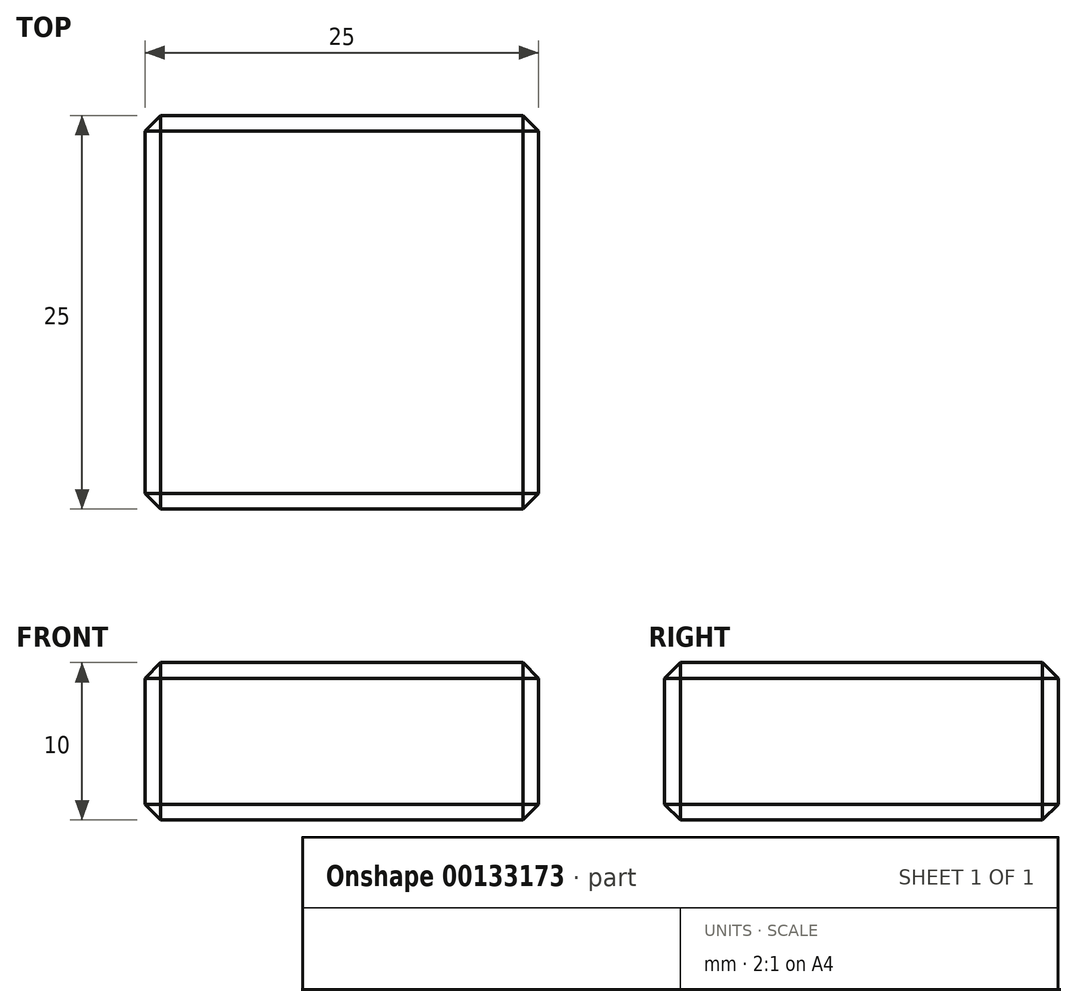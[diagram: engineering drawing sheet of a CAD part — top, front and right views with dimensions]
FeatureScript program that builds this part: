
annotation { "Feature Type Name" : "Feature", "Feature Type Description" : "" }
export const myFeature = defineFeature(function(context is Context, id is Id, definition is map)
    precondition{}
    {
        {
            var Q0;
            Q0=qCreatedBy(makeId("Front.planeOp"),FACE);
            var sketch = newSketch(context, id + "F0", { "sketchPlane" : qUnion([Q0])});
            skLineSegment(sketch, "E0.bottom", {"start": v(-30.6, 0) * mm, "end": v(-5.6, 0) * mm});
            skLineSegment(sketch, "E0.top", {"start": v(-30.6, 10) * mm, "end": v(-5.6, 10) * mm});
            skLineSegment(sketch, "E0.left", {"start": v(-30.6, 0) * mm, "end": v(-30.6, 10) * mm});
            skLineSegment(sketch, "E0.right", {"start": v(-5.6, 0) * mm, "end": v(-5.6, 10) * mm});
            skSolve(sketch);
        }
        {
            var Q0;
            Q0=makeQuery(id+"F0.imprint","IMPRINT",FACE,{"disambiguationData":[TD([[makeQuery(id+"F0.imprint","IMPRINT",EDGE,{"derivedFrom":sQuery(id+"F0.wireOp",EDGE,"E0.bottom")}),1.0]])]});
            extrude(context, id + "F1", {"entities" : qUnion([Q0]), "endBound" : BoundingType.SYMMETRIC, "depth" : 25 * mm});
        }
        {
            var Q0;
            Q0=makeQuery(id+"F1.opExtrude","CAP_EDGE",EDGE,{"disambiguationData":[OSD([sQuery(id+"F0.wireOp",EDGE,"E0.left")])],"isStart":false});
            var Q1;
            Q1=makeQuery(id+"F1.opExtrude","CAP_EDGE",EDGE,{"disambiguationData":[OSD([sQuery(id+"F0.wireOp",EDGE,"E0.right")])],"isStart":false});
            var Q2;
            Q2=makeQuery(id+"F1.opExtrude","CAP_EDGE",EDGE,{"disambiguationData":[OSD([sQuery(id+"F0.wireOp",EDGE,"E0.top")])],"isStart":false});
            var Q3;
            Q3=makeQuery(id+"F1.opExtrude","CAP_EDGE",EDGE,{"disambiguationData":[OSD([sQuery(id+"F0.wireOp",EDGE,"E0.bottom")])],"isStart":false});
            var Q4;
            Q4=makeQuery(id+"F1.opExtrude","SWEPT_EDGE",EDGE,{"disambiguationData":[OSD([sQuery(id+"F0.wireOp",EDGE,"E0.bottom"),sQuery(id+"F0.wireOp",EDGE,"E0.right")])]});
            var Q5;
            Q5=makeQuery(id+"F1.opExtrude","SWEPT_EDGE",EDGE,{"disambiguationData":[OSD([sQuery(id+"F0.wireOp",EDGE,"E0.top"),sQuery(id+"F0.wireOp",EDGE,"E0.right")])]});
            var Q6;
            Q6=makeQuery(id+"F1.opExtrude","CAP_EDGE",EDGE,{"disambiguationData":[OSD([sQuery(id+"F0.wireOp",EDGE,"E0.right")])],"isStart":true});
            var Q7;
            Q7=makeQuery(id+"F1.opExtrude","CAP_EDGE",EDGE,{"disambiguationData":[OSD([sQuery(id+"F0.wireOp",EDGE,"E0.left")])],"isStart":true});
            var Q8;
            Q8=makeQuery(id+"F1.opExtrude","CAP_EDGE",EDGE,{"disambiguationData":[OSD([sQuery(id+"F0.wireOp",EDGE,"E0.top")])],"isStart":true});
            var Q9;
            Q9=makeQuery(id+"F1.opExtrude","CAP_EDGE",EDGE,{"disambiguationData":[OSD([sQuery(id+"F0.wireOp",EDGE,"E0.bottom")])],"isStart":true});
            var Q10;
            Q10=makeQuery(id+"F1.opExtrude","SWEPT_EDGE",EDGE,{"disambiguationData":[OSD([sQuery(id+"F0.wireOp",EDGE,"E0.top"),sQuery(id+"F0.wireOp",EDGE,"E0.left")])]});
            var Q11;
            Q11=makeQuery(id+"F1.opExtrude","SWEPT_EDGE",EDGE,{"disambiguationData":[OSD([sQuery(id+"F0.wireOp",EDGE,"E0.bottom"),sQuery(id+"F0.wireOp",EDGE,"E0.left")])]});
            chamfer(context, id + "F2", {"entities" : qUnion([Q0, Q1, Q2, Q3, Q4, Q5, Q6, Q7, Q8, Q9, Q10, Q11]), "width" : 1 * mm, "tangentPropagation" : true});
        }
    });
